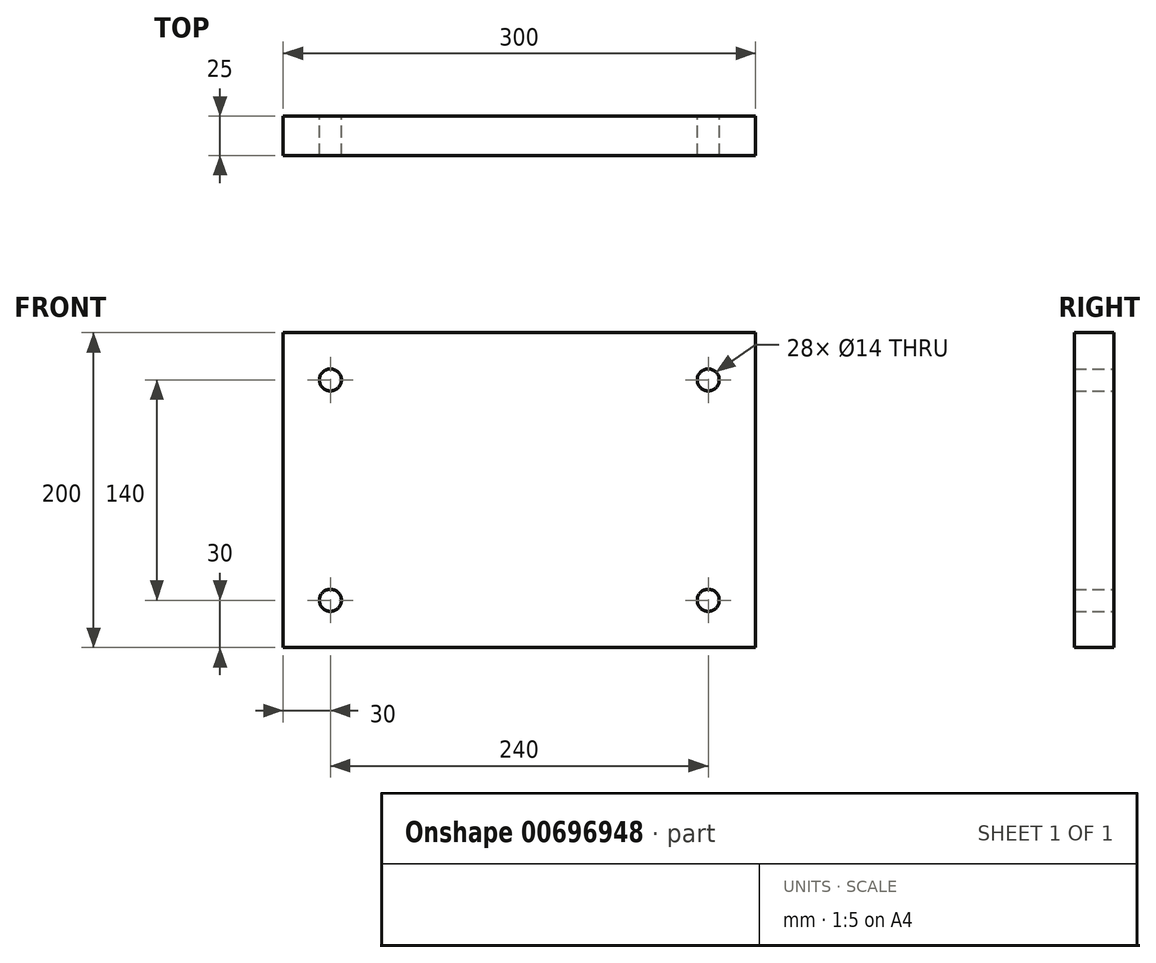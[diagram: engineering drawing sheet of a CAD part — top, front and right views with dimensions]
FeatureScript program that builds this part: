
annotation { "Feature Type Name" : "Feature", "Feature Type Description" : "" }
export const myFeature = defineFeature(function(context is Context, id is Id, definition is map)
    precondition{}
    {
        {
            var Q0;
            Q0=qCreatedBy(makeId("Front.planeOp"),FACE);
            var sketch = newSketch(context, id + "F0", { "sketchPlane" : qUnion([Q0])});
            skLineSegment(sketch, "E0.bottom", {"start": v(150, 100) * mm, "end": v(-150, 100) * mm});
            skLineSegment(sketch, "E0.top", {"start": v(150, -100) * mm, "end": v(-150, -100) * mm});
            skLineSegment(sketch, "E0.left", {"start": v(150, 100) * mm, "end": v(150, -100) * mm});
            skLineSegment(sketch, "E0.right", {"start": v(-150, 100) * mm, "end": v(-150, -100) * mm});
            skPoint(sketch, "E0.middle", {"position": v(0, 0) * mm});
            skLineSegment(sketch, "E1.bottom", {"start": v(120, 70) * mm, "end": v(-120, 70) * mm});
            skLineSegment(sketch, "E1.top", {"start": v(120, -70) * mm, "end": v(-120, -70) * mm});
            skLineSegment(sketch, "E1.left", {"start": v(120, 70) * mm, "end": v(120, -70) * mm});
            skLineSegment(sketch, "E1.right", {"start": v(-120, 70) * mm, "end": v(-120, -70) * mm});
            skCircle(sketch, "E2", {"center": v(120, 70) * mm, "radius": 7 * mm});
            skCircle(sketch, "E3", {"center": v(120, -70) * mm, "radius": 7 * mm});
            skCircle(sketch, "E4", {"center": v(-120, -70) * mm, "radius": 7 * mm});
            skCircle(sketch, "E5", {"center": v(-120, 70) * mm, "radius": 7 * mm});
            skSolve(sketch);
        }
        {
            var Q0;
            {var subQ5=sQuery(id+"F0.wireOp",EDGE,"E2");var subQ13=sQuery(id+"F0.wireOp",EDGE,"E1.bottom");var subQ14=makeQuery(id+"F0.imprint","INTERSECT",VERTEX,{"derivedFrom":[subQ13,subQ5]});Q0=makeQuery(id+"F0.imprint","IMPRINT",FACE,{"disambiguationData":[TD([[makeQuery(id+"F0.imprint","IMPRINT",EDGE,{"disambiguationData":[TD([[subQ14,-1.0]])],"derivedFrom":subQ13}),1.0]])]});}
            var Q1;
            Q1=makeQuery(id+"F0.imprint","IMPRINT",FACE,{"disambiguationData":[TD([[makeQuery(id+"F0.imprint","IMPRINT",EDGE,{"derivedFrom":sQuery(id+"F0.wireOp",EDGE,"E0.bottom")}),1.0]])]});
            extrude(context, id + "F1", {"entities" : qUnion([Q0, Q1]), "depth" : 25 * mm, "offsetDistance" : 25 * mm});
        }
    });
